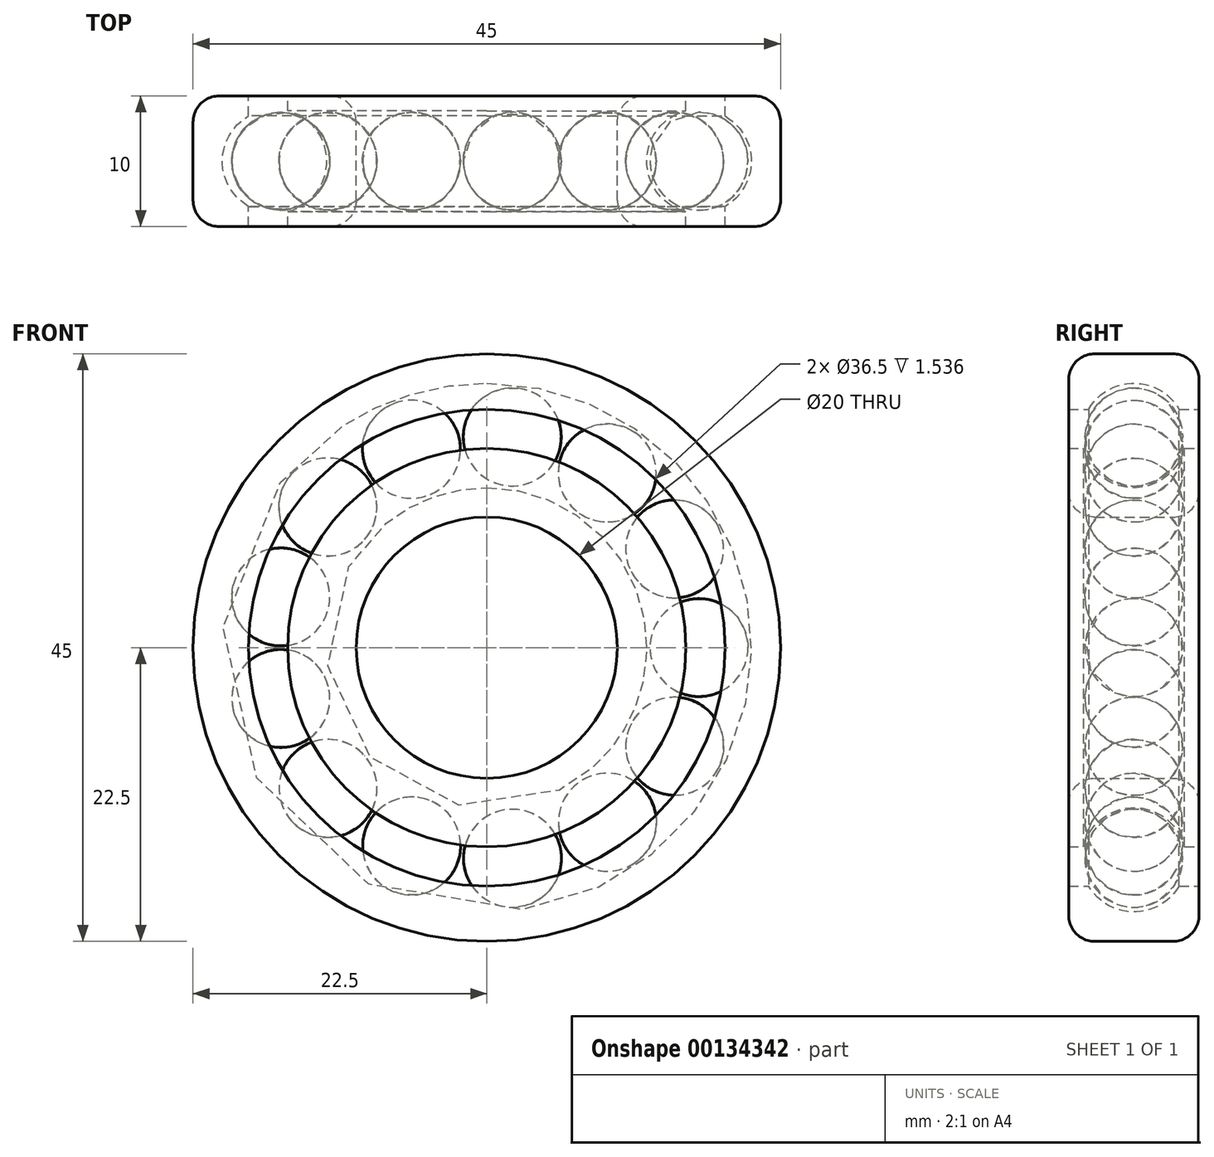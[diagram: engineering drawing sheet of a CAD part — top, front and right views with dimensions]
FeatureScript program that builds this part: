
annotation { "Feature Type Name" : "Feature", "Feature Type Description" : "" }
export const myFeature = defineFeature(function(context is Context, id is Id, definition is map)
    precondition{}
    {
        {
            var Q0;
            Q0=qCreatedBy(makeId("Front.planeOp"),FACE);
            var sketch = newSketch(context, id + "F0", { "sketchPlane" : qUnion([Q0])});
            skCircle(sketch, "E0", {"center": v(0, 0) * mm, "radius": 10 * mm});
            skCircle(sketch, "E1", {"center": v(0, 0) * mm, "radius": 22.5 * mm});
            skCircle(sketch, "E2", {"center": v(0, 0) * mm, "radius": 16.25 * mm});
            skCircle(sketch, "E3.0", {"center": v(0, 0) * mm, "radius": 18.25 * mm});
            skCircle(sketch, "E4.0", {"center": v(0, 0) * mm, "radius": 15.25 * mm});
            skSolve(sketch);
        }
        {
            var Q0;
            Q0=makeQuery(id+"F0.imprint","IMPRINT",FACE,{"disambiguationData":[TD([[makeQuery(id+"F0.imprint","IMPRINT",EDGE,{"derivedFrom":sQuery(id+"F0.wireOp",EDGE,"E0")}),-1.0]])]});
            var Q1;
            Q1=makeQuery(id+"F0.imprint","IMPRINT",FACE,{"disambiguationData":[TD([[makeQuery(id+"F0.imprint","IMPRINT",EDGE,{"derivedFrom":sQuery(id+"F0.wireOp",EDGE,"E1")}),1.0]])]});
            extrude(context, id + "F1", {"entities" : qUnion([Q0, Q1]), "depth" : 10 * mm});
        }
        {
            var Q0;
            Q0=qCreatedBy(makeId("Top.planeOp"),FACE);
            var sketch = newSketch(context, id + "F2", { "sketchPlane" : qUnion([Q0])});
            skCircle(sketch, "E5", {"center": v(-16.25, -5) * mm, "radius": 4 * mm});
            skLineSegment(sketch, "E6", {"start": v(0, -24.56) * mm, "end": v(0, 17.21) * mm, "construction": true});
            skSolve(sketch);
        }
        {
            var Q0;
            Q0 = qSketchRegion(id + "F2", true);
            var Q1;
            Q1=sQuery(id+"F2.wireOp",EDGE,"E6");
            revolve(context, id + "F3", {"operationType" : NewBodyOperationType.REMOVE, "entities" : qUnion([Q0]), "axis" : qUnion([Q1]), "revolveType" : RevolveType.FULL, "oppositeDirection" : true});
        }
        {
            var Q0;
            Q0=qCreatedBy(makeId("Front.planeOp"),FACE);
            var sketch = newSketch(context, id + "F4", { "sketchPlane" : qUnion([Q0])});
            skArc(sketch, "E7", {"start": v(20, 0) * mm, "mid": v(16.25, 3.75) * mm, "end": v(12.5, 0) * mm});
            skLineSegment(sketch, "E8", {"start": v(20, 0) * mm, "end": v(12.5, 0) * mm});
            skSolve(sketch);
        }
        {
            var Q0;
            Q0 = qSketchRegion(id + "F4", true);
            var Q1;
            Q1=sQuery(id+"F4.wireOp",EDGE,"E8");
            revolve(context, id + "F5", {"entities" : qUnion([Q0]), "axis" : qUnion([Q1]), "revolveType" : RevolveType.FULL});
        }
        {
            var Q0;
            Q0=makeQuery(id+"F5.opRevolve","SWEPT_BODY",BODY,{"disambiguationData":[OSD([sQuery(id+"F4.wireOp",EDGE,"E7"),sQuery(id+"F4.wireOp",EDGE,"E8")])]});
            transform(context, id + "F6", {"entities" : qUnion([Q0]), "transformType" : TransformType.TRANSLATION_3D, "dx" : 0 * mm, "dy" : -5 * mm, "dz" : 0 * mm, "makeCopy" : false});
        }
        {
            var Q0;
            Q0=qCreatedBy(makeId("Top.planeOp"),FACE);
            var sketch = newSketch(context, id + "F7", { "sketchPlane" : qUnion([Q0])});
            skLineSegment(sketch, "E9", {"start": v(0, -23.65) * mm, "end": v(0, 20.5) * mm, "construction": true});
            skSolve(sketch);
        }
        {
            var Q0;
            Q0=makeQuery(id+"F5.opRevolve","SWEPT_BODY",BODY,{"disambiguationData":[OSD([sQuery(id+"F4.wireOp",EDGE,"E7"),sQuery(id+"F4.wireOp",EDGE,"E8")])]});
            var Q1;
            Q1=sQuery(id+"F7.wireOp",EDGE,"E9");
            circularPattern(context, id + "F8", {"entities" : qUnion([Q0]), "axis" : qUnion([Q1]), "angle" : 27.7 * degree, "instanceCount" : 13});
        }
        {
            var Q0;
            Q0=makeQuery(id+"F1.opExtrude","CAP_EDGE",EDGE,{"disambiguationData":[OSD([sQuery(id+"F0.wireOp",EDGE,"E1")])],"isStart":false});
            var Q1;
            Q1=makeQuery(id+"F1.opExtrude","CAP_EDGE",EDGE,{"disambiguationData":[OSD([sQuery(id+"F0.wireOp",EDGE,"E1")])],"isStart":true});
            var Q2;
            Q2=makeQuery(id+"F1.opExtrude","CAP_EDGE",EDGE,{"disambiguationData":[OSD([sQuery(id+"F0.wireOp",EDGE,"E0")])],"isStart":false});
            var Q3;
            Q3=makeQuery(id+"F1.opExtrude","CAP_EDGE",EDGE,{"disambiguationData":[OSD([sQuery(id+"F0.wireOp",EDGE,"E0")])],"isStart":true});
            fillet(context, id + "F9", {"entities" : qUnion([Q0, Q1, Q2, Q3]), "radius" : 2 * mm, "allowEdgeOverflow" : false});
        }
    });
